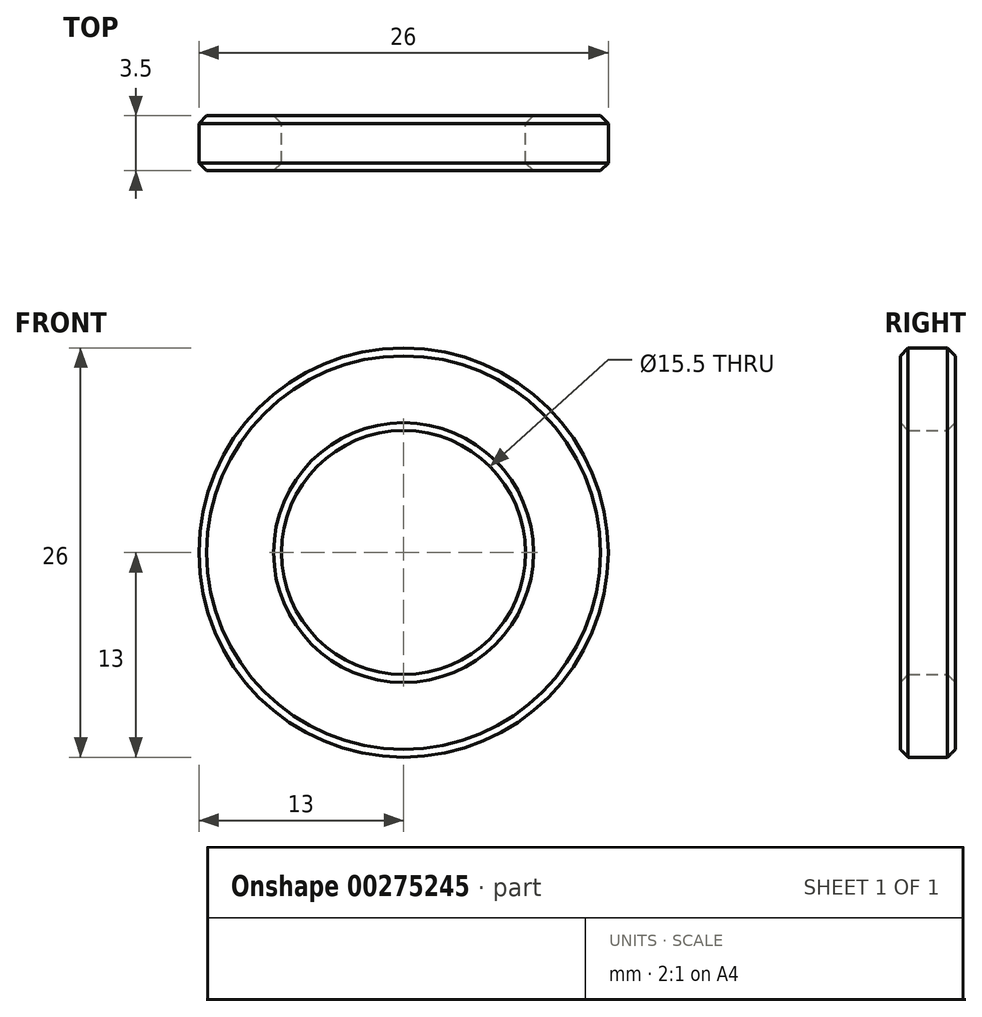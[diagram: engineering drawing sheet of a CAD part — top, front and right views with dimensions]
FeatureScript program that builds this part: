
annotation { "Feature Type Name" : "Feature", "Feature Type Description" : "" }
export const myFeature = defineFeature(function(context is Context, id is Id, definition is map)
    precondition{}
    {
        {
            var Q0;
            Q0=qCreatedBy(makeId("Front.planeOp"),FACE);
            var sketch = newSketch(context, id + "F0", { "sketchPlane" : qUnion([Q0])});
            skCircle(sketch, "E0", {"center": v(0, 0) * mm, "radius": 7.75 * mm});
            skCircle(sketch, "E1", {"center": v(0, 0) * mm, "radius": 13 * mm});
            skSolve(sketch);
        }
        {
            var Q0;
            Q0 = qSketchRegion(id + "F0", true);
            extrude(context, id + "F1", {"entities" : qUnion([Q0]), "depth" : 3.5 * mm});
        }
        {
            var Q0;
            Q0=makeQuery(id+"F1.opExtrude","CAP_EDGE",EDGE,{"disambiguationData":[OSD([sQuery(id+"F0.wireOp",EDGE,"E1")])],"isStart":false});
            var Q1;
            Q1=makeQuery(id+"F1.opExtrude","CAP_EDGE",EDGE,{"disambiguationData":[OSD([sQuery(id+"F0.wireOp",EDGE,"E0")])],"isStart":false});
            var Q2;
            Q2=makeQuery(id+"F1.opExtrude","CAP_EDGE",EDGE,{"disambiguationData":[OSD([sQuery(id+"F0.wireOp",EDGE,"E1")])],"isStart":true});
            var Q3;
            Q3=makeQuery(id+"F1.opExtrude","CAP_EDGE",EDGE,{"disambiguationData":[OSD([sQuery(id+"F0.wireOp",EDGE,"E0")])],"isStart":true});
            chamfer(context, id + "F2", {"entities" : qUnion([Q0, Q1, Q2, Q3]), "chamferType" : ChamferType.OFFSET_ANGLE, "width" : .5 * mm, "oppositeDirection" : false, "angle" : 45 * degree, "tangentPropagation" : true});
        }
    });
